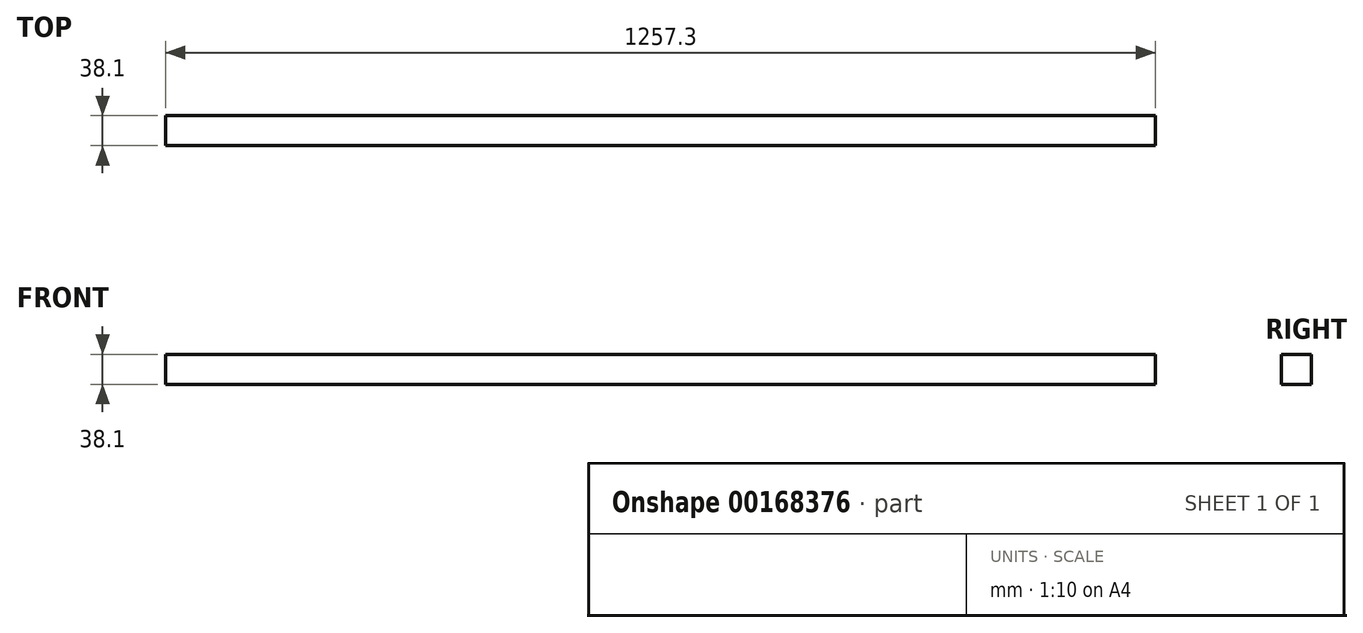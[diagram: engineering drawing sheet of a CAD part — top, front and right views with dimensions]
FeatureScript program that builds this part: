
annotation { "Feature Type Name" : "Feature", "Feature Type Description" : "" }
export const myFeature = defineFeature(function(context is Context, id is Id, definition is map)
    precondition{}
    {
        {
            var Q0;
            Q0=qCreatedBy(makeId("Top.planeOp"),FACE);
            var sketch = newSketch(context, id + "F0", { "sketchPlane" : qUnion([Q0])});
            skLineSegment(sketch, "E0.bottom", {"start": v(-628.65, 19.05) * mm, "end": v(628.65, 19.05) * mm});
            skLineSegment(sketch, "E0.top", {"start": v(-628.65, -19.05) * mm, "end": v(628.65, -19.05) * mm});
            skLineSegment(sketch, "E0.left", {"start": v(-628.65, 19.05) * mm, "end": v(-628.65, -19.05) * mm});
            skLineSegment(sketch, "E0.right", {"start": v(628.65, 19.05) * mm, "end": v(628.65, -19.05) * mm});
            skPoint(sketch, "E0.middle", {"position": v(0, 0) * mm});
            skSolve(sketch);
        }
        {
            var Q0;
            Q0 = qSketchRegion(id + "F0", true);
            extrude(context, id + "F1", {"entities" : qUnion([Q0]), "depth" : 38.1 * mm});
        }
    });
